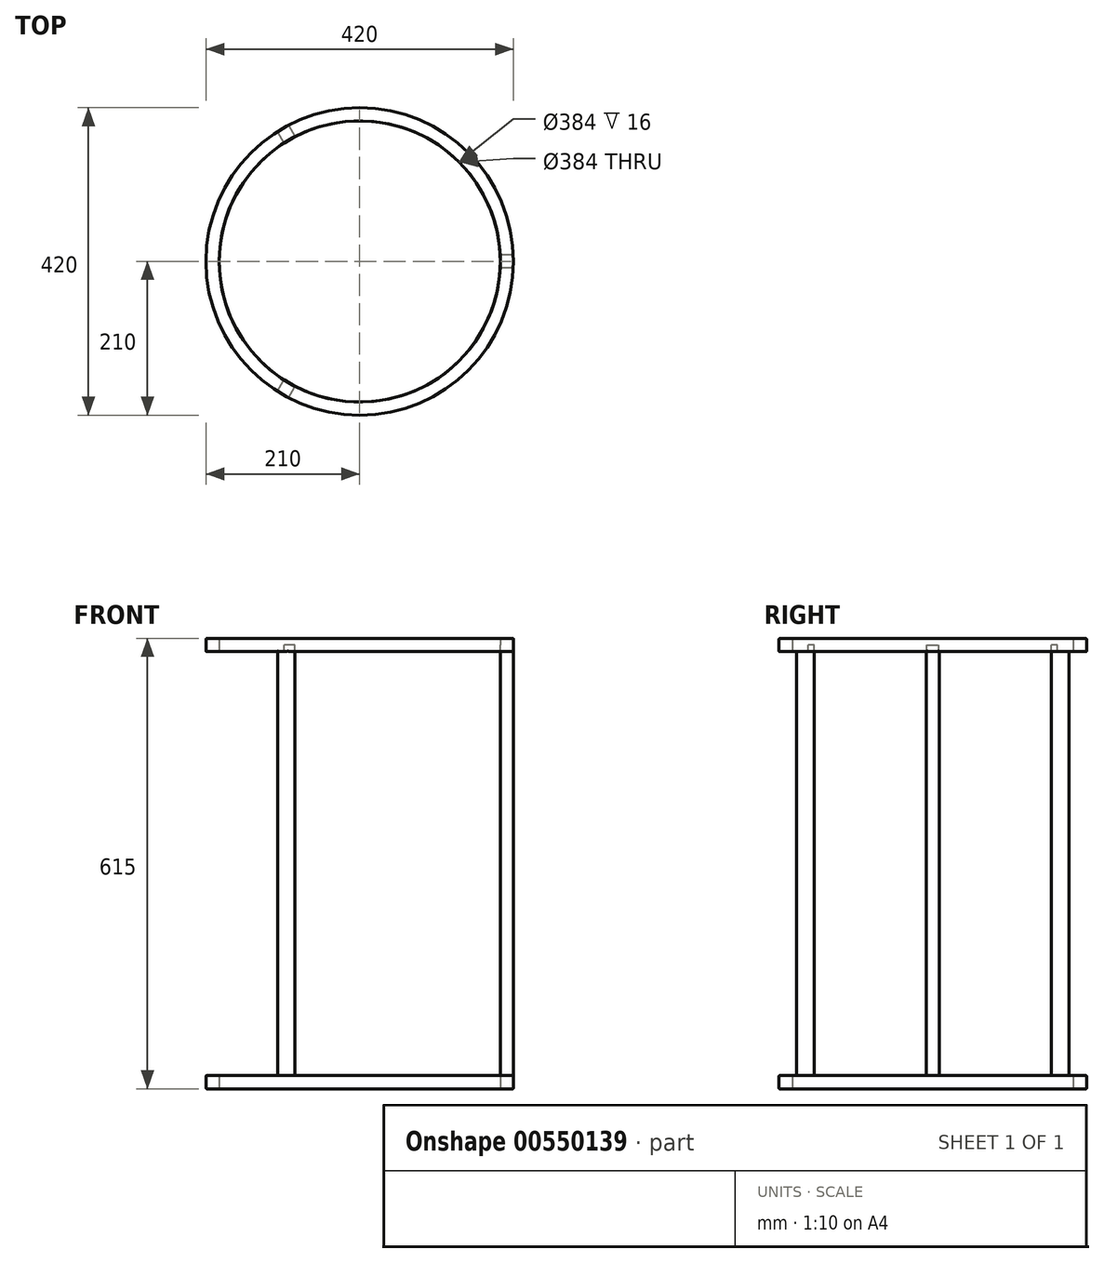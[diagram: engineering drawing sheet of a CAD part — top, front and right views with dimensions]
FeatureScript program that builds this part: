
annotation { "Feature Type Name" : "Feature", "Feature Type Description" : "" }
export const myFeature = defineFeature(function(context is Context, id is Id, definition is map)
    precondition{}
    {
        {
            var Q0;
            Q0=qCreatedBy(makeId("Front.planeOp"),FACE);
            var sketch = newSketch(context, id + "F0", { "sketchPlane" : qUnion([Q0])});
            skLineSegment(sketch, "E0.bottom", {"start": v(209, -9) * mm, "end": v(193, -9) * mm});
            skLineSegment(sketch, "E0.top", {"start": v(209, 9) * mm, "end": v(193, 9) * mm});
            skLineSegment(sketch, "E0.left", {"start": v(210, -8) * mm, "end": v(210, 8) * mm});
            skLineSegment(sketch, "E0.right", {"start": v(192, -8) * mm, "end": v(192, 8) * mm});
            skPoint(sketch, "E1.visualSharp", {"position": v(192, 9) * mm});
            skArc(sketch, "E1.filletArc", {"start": v(193, 9) * mm, "mid": v(192.3, 8.7) * mm, "end": v(192, 8) * mm});
            skPoint(sketch, "E2.visualSharp", {"position": v(210, 9) * mm});
            skArc(sketch, "E2.filletArc", {"start": v(210, 8) * mm, "mid": v(209.7, 8.7) * mm, "end": v(209, 9) * mm});
            skArc(sketch, "E3.filletArc", {"start": v(209, -9) * mm, "mid": v(209.7, -8.7) * mm, "end": v(210, -8) * mm});
            skPoint(sketch, "E4.visualSharp", {"position": v(192, -9) * mm});
            skArc(sketch, "E4.filletArc", {"start": v(192, -8) * mm, "mid": v(192.3, -8.7) * mm, "end": v(193, -9) * mm});
            skLineSegment(sketch, "E5", {"start": v(0, 0) * mm, "end": v(0, 20) * mm, "construction": true});
            skPoint(sketch, "E6", {"position": v(210, 0) * mm});
            skSolve(sketch);
        }
        {
            var Q0;
            Q0=qSketchRegion(id+"F0",true);
            var Q1;
            Q1=sQuery(id+"F0.wireOp",EDGE,"E5");
            revolve(context, id + "F1", {"entities" : qUnion([Q0]), "axis" : qUnion([Q1]), "revolveType" : RevolveType.FULL});
        }
        {
            var Q0;
            Q0=qCreatedBy(makeId("Top.planeOp"),FACE);
            var sketch = newSketch(context, id + "F2", { "sketchPlane" : qUnion([Q0])});
            skLineSegment(sketch, "E7.bottom", {"start": v(208.8, -9) * mm, "end": v(192.8, -9) * mm});
            skLineSegment(sketch, "E7.top", {"start": v(208.8, 9) * mm, "end": v(192.8, 9) * mm});
            skLineSegment(sketch, "E7.left", {"start": v(209.8, -8) * mm, "end": v(209.8, 8) * mm});
            skLineSegment(sketch, "E7.right", {"start": v(191.8, -8) * mm, "end": v(191.8, 8) * mm});
            skPoint(sketch, "E7.middle", {"position": v(200.8, 0) * mm});
            skPoint(sketch, "E8", {"position": v(209.8, 0) * mm});
            skPoint(sketch, "E9.visualSharp", {"position": v(209.8, -9) * mm});
            skArc(sketch, "E9.filletArc", {"start": v(208.8, -9) * mm, "mid": v(209.51, -8.7) * mm, "end": v(209.8, -8) * mm});
            skPoint(sketch, "E10.visualSharp", {"position": v(209.8, 9) * mm});
            skArc(sketch, "E10.filletArc", {"start": v(209.8, 8) * mm, "mid": v(209.51, 8.7) * mm, "end": v(208.8, 9) * mm});
            skPoint(sketch, "E11.visualSharp", {"position": v(191.8, -9) * mm});
            skArc(sketch, "E11.filletArc", {"start": v(191.8, -8) * mm, "mid": v(192.1, -8.7) * mm, "end": v(192.8, -9) * mm});
            skPoint(sketch, "E12.visualSharp", {"position": v(191.8, 9) * mm});
            skArc(sketch, "E12.filletArc", {"start": v(192.8, 9) * mm, "mid": v(192.1, 8.7) * mm, "end": v(191.8, 8) * mm});
            skLineSegment(sketch, "E13.1.0", {"start": v(-96.6, 185.33) * mm, "end": v(-88.6, 171.48) * mm});
            skArc(sketch, "E13.1.1", {"start": v(-96.6, 185.33) * mm, "mid": v(-97.22, 185.8) * mm, "end": v(-97.97, 185.7) * mm});
            skLineSegment(sketch, "E13.1.2", {"start": v(-97.97, 185.7) * mm, "end": v(-111.83, 177.7) * mm});
            skArc(sketch, "E13.1.3", {"start": v(-111.83, 177.7) * mm, "mid": v(-112.3, 177.1) * mm, "end": v(-112.2, 176.33) * mm});
            skLineSegment(sketch, "E13.1.4", {"start": v(-112.2, 176.33) * mm, "end": v(-104.2, 162.48) * mm});
            skArc(sketch, "E13.1.5", {"start": v(-104.2, 162.48) * mm, "mid": v(-103.6, 162) * mm, "end": v(-102.83, 162.1) * mm});
            skLineSegment(sketch, "E13.1.6", {"start": v(-88.97, 170.1) * mm, "end": v(-102.83, 162.1) * mm});
            skArc(sketch, "E13.1.7", {"start": v(-88.97, 170.1) * mm, "mid": v(-88.5, 170.72) * mm, "end": v(-88.6, 171.48) * mm});
            skLineSegment(sketch, "E13.2.0", {"start": v(-112.2, -176.33) * mm, "end": v(-104.2, -162.48) * mm});
            skArc(sketch, "E13.2.1", {"start": v(-112.2, -176.33) * mm, "mid": v(-112.3, -177.1) * mm, "end": v(-111.83, -177.7) * mm});
            skLineSegment(sketch, "E13.2.2", {"start": v(-111.83, -177.7) * mm, "end": v(-97.97, -185.7) * mm});
            skArc(sketch, "E13.2.3", {"start": v(-97.97, -185.7) * mm, "mid": v(-97.22, -185.8) * mm, "end": v(-96.6, -185.33) * mm});
            skLineSegment(sketch, "E13.2.4", {"start": v(-96.6, -185.33) * mm, "end": v(-88.6, -171.48) * mm});
            skArc(sketch, "E13.2.5", {"start": v(-88.6, -171.48) * mm, "mid": v(-88.5, -170.72) * mm, "end": v(-88.97, -170.1) * mm});
            skLineSegment(sketch, "E13.2.6", {"start": v(-102.83, -162.1) * mm, "end": v(-88.97, -170.1) * mm});
            skArc(sketch, "E13.2.7", {"start": v(-102.83, -162.1) * mm, "mid": v(-103.6, -162) * mm, "end": v(-104.2, -162.48) * mm});
            skPoint(sketch, "E13.center", {"position": v(0, 0) * mm});
            skSolve(sketch);
        }
        {
            var Q0;
            Q0=qSketchRegion(id+"F2",true);
            extrude(context, id + "F3", {"entities" : qUnion([Q0]), "operationType" : NewBodyOperationType.ADD, "oppositeDirection" : true, "depth" : ((300 * 2) - 12) * mm, "offsetDistance" : 25 * mm});
        }
        {
            var Q0;
            Q0=qCreatedBy(makeId("Front.planeOp"),FACE);
            var sketch = newSketch(context, id + "F4", { "sketchPlane" : qUnion([Q0])});
            skLineSegment(sketch, "E14.bottom", {"start": v(209, -606) * mm, "end": v(193, -606) * mm});
            skLineSegment(sketch, "E14.top", {"start": v(209, -588) * mm, "end": v(193, -588) * mm});
            skLineSegment(sketch, "E14.left", {"start": v(210, -605) * mm, "end": v(210, -589) * mm});
            skLineSegment(sketch, "E14.right", {"start": v(192, -605) * mm, "end": v(192, -589) * mm});
            skPoint(sketch, "E15.visualSharp", {"position": v(192, -588) * mm});
            skArc(sketch, "E15.filletArc", {"start": v(193, -588) * mm, "mid": v(192.3, -588.3) * mm, "end": v(192, -589) * mm});
            skPoint(sketch, "E16.visualSharp", {"position": v(210, -588) * mm});
            skArc(sketch, "E16.filletArc", {"start": v(210, -589) * mm, "mid": v(209.7, -588.3) * mm, "end": v(209, -588) * mm});
            skArc(sketch, "E17.filletArc", {"start": v(209, -606) * mm, "mid": v(209.7, -605.7) * mm, "end": v(210, -605) * mm});
            skPoint(sketch, "E18.visualSharp", {"position": v(192, -606) * mm});
            skArc(sketch, "E18.filletArc", {"start": v(192, -605) * mm, "mid": v(192.3, -605.7) * mm, "end": v(193, -606) * mm});
            skPoint(sketch, "E19", {"position": v(210, -597) * mm});
            skSolve(sketch);
        }
        {
            var Q0;
            Q0=qSketchRegion(id+"F4",true);
            var Q1;
            Q1=sQuery(id+"F0.wireOp",EDGE,"E5");
            revolve(context, id + "F5", {"operationType" : NewBodyOperationType.ADD, "entities" : qUnion([Q0]), "axis" : qUnion([Q1]), "revolveType" : RevolveType.FULL});
        }
    });
